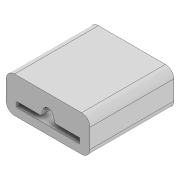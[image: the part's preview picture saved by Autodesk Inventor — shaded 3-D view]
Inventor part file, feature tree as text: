
AUTODESK INVENTOR PART (.ipt)
format: ipt  version: 2022 (Build 260153000, 153)  size: 109,568 bytes
history: native  units: mm
features: extrude x1, fillet x1, sketch x1
ambient origin geometry x8: Origin, YZ Plane, XZ Plane, XY Plane, X Axis, Y Axis, Z Axis, Center Point
bodies: Solid1 (feature_tree)
feature tree (3):
  extrude  "Extrusion1"  Depth=7.5mm
  fillet  "Fillet1"  Radius=3.75mm
  sketch  "Sketch1"  dims[d0=10.0mm d1=7.5mm d2=3.75mm d3=5.0mm d4=1.0mm d5=0.6mm d6=1.2mm d7=1.5mm d8=12.217305mm d9=12.217305mm d10=10.0mm d11=0.0mm d12=1.0mm]
